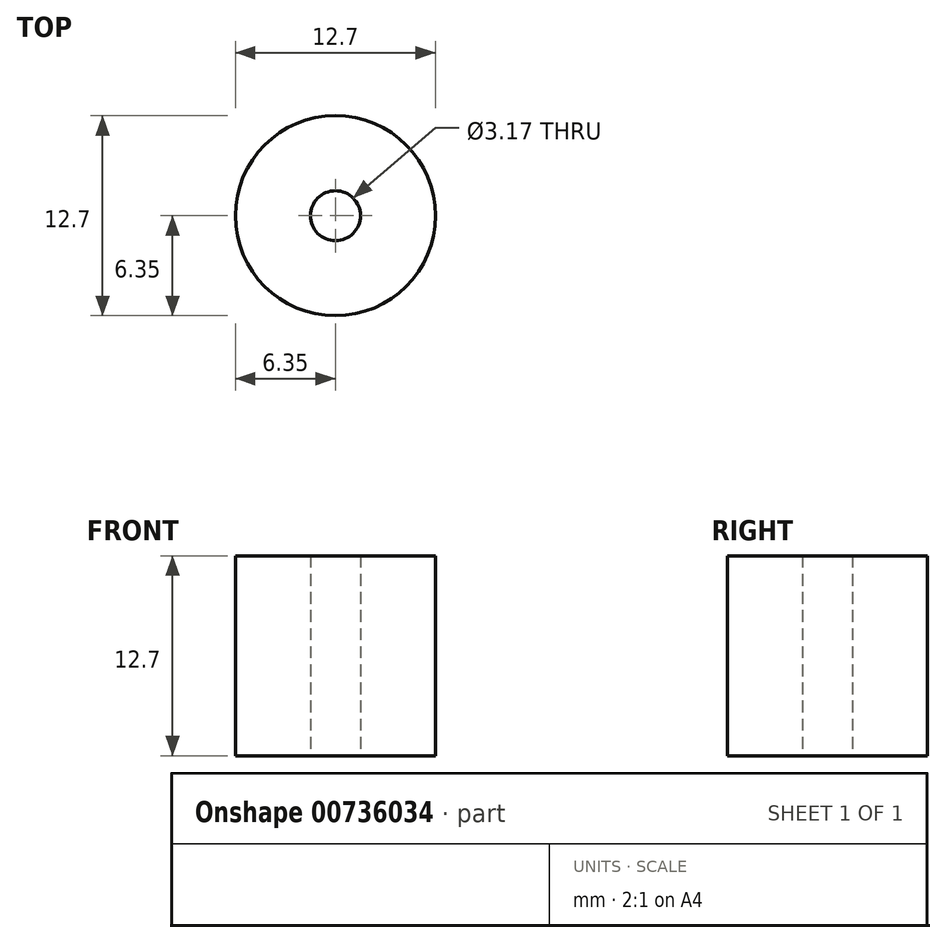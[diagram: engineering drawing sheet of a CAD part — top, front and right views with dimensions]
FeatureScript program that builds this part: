
annotation { "Feature Type Name" : "Feature", "Feature Type Description" : "" }
export const myFeature = defineFeature(function(context is Context, id is Id, definition is map)
    precondition{}
    {
        {
            var Q0;
            Q0=qCreatedBy(makeId("Top.planeOp"),FACE);
            var sketch = newSketch(context, id + "F0", { "sketchPlane" : qUnion([Q0])});
            skCircle(sketch, "E0", {"center": v(0, 0) * mm, "radius": 1.59 * mm});
            skCircle(sketch, "E1", {"center": v(0, 0) * mm, "radius": 6.35 * mm});
            skSolve(sketch);
        }
        {
            var Q0;
            Q0 = qSketchRegion(id + "F0", true);
            extrude(context, id + "F1", {"entities" : qUnion([Q0]), "depth" : 12.7 * mm, "offsetDistance" : 25 * mm});
        }
    });
